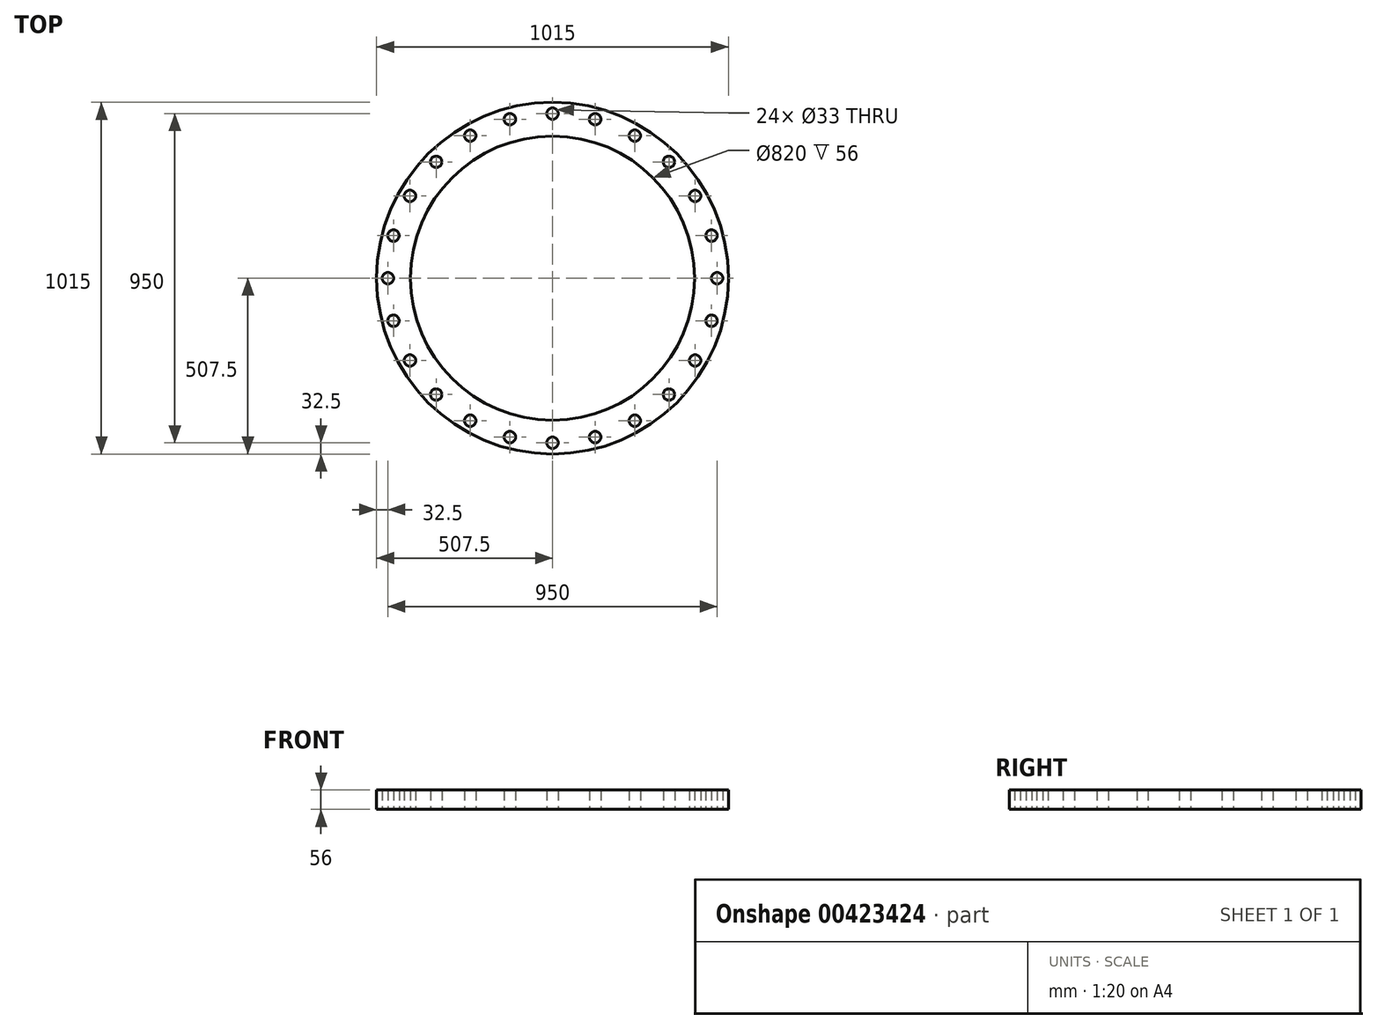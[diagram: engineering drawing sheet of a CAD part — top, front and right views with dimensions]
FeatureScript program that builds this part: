
annotation { "Feature Type Name" : "Feature", "Feature Type Description" : "" }
export const myFeature = defineFeature(function(context is Context, id is Id, definition is map)
    precondition{}
    {
        {
            var Q0;
            Q0=qCreatedBy(makeId("Top.planeOp"),FACE);
            var sketch = newSketch(context, id + "F0", { "sketchPlane" : qUnion([Q0])});
            skCircle(sketch, "E0", {"center": v(0, 0) * mm, "radius": 507.5 * mm});
            skCircle(sketch, "E1", {"center": v(0, 0) * mm, "radius": 410 * mm});
            skCircle(sketch, "E2", {"center": v(475, 0) * mm, "radius": 16.5 * mm});
            skCircle(sketch, "E3.1.0", {"center": v(458.81, 122.94) * mm, "radius": 16.5 * mm});
            skCircle(sketch, "E3.2.0", {"center": v(411.36, 237.5) * mm, "radius": 16.5 * mm});
            skCircle(sketch, "E3.3.0", {"center": v(335.88, 335.88) * mm, "radius": 16.5 * mm});
            skCircle(sketch, "E3.4.0", {"center": v(237.5, 411.36) * mm, "radius": 16.5 * mm});
            skCircle(sketch, "E3.5.0", {"center": v(122.94, 458.81) * mm, "radius": 16.5 * mm});
            skCircle(sketch, "E3.6.0", {"center": v(0, 475) * mm, "radius": 16.5 * mm});
            skCircle(sketch, "E3.7.0", {"center": v(-122.94, 458.81) * mm, "radius": 16.5 * mm});
            skCircle(sketch, "E3.8.0", {"center": v(-237.5, 411.36) * mm, "radius": 16.5 * mm});
            skCircle(sketch, "E3.9.0", {"center": v(-335.88, 335.88) * mm, "radius": 16.5 * mm});
            skCircle(sketch, "E3.10.0", {"center": v(-411.36, 237.5) * mm, "radius": 16.5 * mm});
            skCircle(sketch, "E3.11.0", {"center": v(-458.81, 122.94) * mm, "radius": 16.5 * mm});
            skCircle(sketch, "E3.12.0", {"center": v(-475, 0) * mm, "radius": 16.5 * mm});
            skCircle(sketch, "E3.13.0", {"center": v(-458.81, -122.94) * mm, "radius": 16.5 * mm});
            skCircle(sketch, "E3.14.0", {"center": v(-411.36, -237.5) * mm, "radius": 16.5 * mm});
            skCircle(sketch, "E3.15.0", {"center": v(-335.88, -335.88) * mm, "radius": 16.5 * mm});
            skCircle(sketch, "E4.1.16.0", {"center": v(-237.5, -411.36) * mm, "radius": 16.5 * mm});
            skCircle(sketch, "E4.1.17.0", {"center": v(-122.94, -458.81) * mm, "radius": 16.5 * mm});
            skCircle(sketch, "E4.1.18.0", {"center": v(0, -475) * mm, "radius": 16.5 * mm});
            skCircle(sketch, "E4.1.19.0", {"center": v(122.94, -458.81) * mm, "radius": 16.5 * mm});
            skCircle(sketch, "E4.1.20.0", {"center": v(237.5, -411.36) * mm, "radius": 16.5 * mm});
            skCircle(sketch, "E4.1.21.0", {"center": v(335.88, -335.88) * mm, "radius": 16.5 * mm});
            skCircle(sketch, "E4.1.22.0", {"center": v(411.36, -237.5) * mm, "radius": 16.5 * mm});
            skCircle(sketch, "E4.1.23.0", {"center": v(458.81, -122.94) * mm, "radius": 16.5 * mm});
            skSolve(sketch);
        }
        {
            var Q0;
            Q0=makeQuery(id+"F0.imprint","IMPRINT",FACE,{"disambiguationData":[TD([[makeQuery(id+"F0.imprint","IMPRINT",EDGE,{"derivedFrom":sQuery(id+"F0.wireOp",EDGE,"E0")}),1.0]])]});
            extrude(context, id + "F1", {"entities" : qUnion([Q0]), "depth" : 56 * mm});
        }
    });
